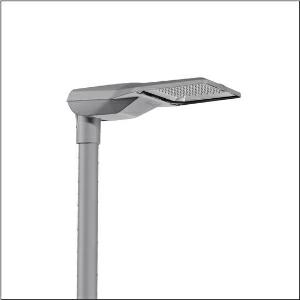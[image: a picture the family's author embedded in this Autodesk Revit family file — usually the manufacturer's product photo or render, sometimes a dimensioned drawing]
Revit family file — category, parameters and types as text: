
# Revit family: streetlight_sl_21_iq_midi___st1_0a_5xe3d31g08mb_3419
name_source: partatom
category: Lighting Fixtures
units: mm (PartAtom-declared; Revit-internal decimal feet)

## family parameters
Cut with Voids When Loaded = No
Host = Face
Light Source = No
Part Type = Normal
Room Calculation Point = No
Round Connector Dimension = Use Diameter
Shared = No

## types (1)
- --- (1 x LED, 19500 lm, 146.7 W, 3000K)
    Apparent Load = 147 VA
    CIE Flux Codes = 37 72 97 100 100
    Color Rendering = 70
    Color Temperature = 3000K
    Default Elevation = 1800 mm
    Description = Streetlight SL 21 iQ midi, mast luminaire, primary light control with lens, of PMMA, primary optical cover: cover, of toughened safety glass, transparent, light distribution: ST1.0a, light emission: direct distribution, primary light characteristic: asymmetric, installation type: post-top, side-entry, LED, High Power LED, rated luminous flux: 19.500lm, luminous efficacy: 133lm/W, light colour: 730, colour temperature: 3000K, control gear: iQ Street-Remote, control: Street-Remote, Auto-Match, Temp-Guard, Lumen-Switch, Night-Set, Smart-Wire, Light-Fading, Desk-Remote (wireless, voltage-free reading and setting of iQ features in the workshop via application-optimized NFC function/RFID function), optimised constant luminous flux control (CLO 2.0), pre-setting: linear dimming characteristic, mains connection: 230..240V, AC, 50/60Hz, start of lifetime: 147W, end of service life: 161W, reduction: 62W, luminaire housing, of diecast aluminium, powder-coated, Siteco® metallic grey (DB 702S), corrosivity category C5 high according to DIN EN ISO 12944, please order mast flange separately, inclination adjustable: 0°, 5°, 10°, 15°, sealing non-destructively replaceable, multi-level sealing system, length: 644mm, width: 335mm, height: 110mm, mast flange for spigot size: 42mm (side-entry): 5XC10008XM4, 60/48mm (side-entry/post-top): 5XC10108XM2, 76/60mm (side-entry/post-top): 5XC10108XM1, mounting height: 4..8m, protection rating (complete): IP66, insulation class (complete): insulation class II (safety insulation), certification: CE, ENEC, ENEC+, VDE, impact resistance: IK10, permissible operating ambient temperature for outdoor applications: -40..+50°C, standard-compliant lighting for roads and squares, packaging unit: 1 piece

Light Distribution: ST1.0a
    Height = 111 mm
    Lamp = 1 x LED
    Lamp Light Flux = 19500 lm
    Lamp Power = 146.7 W
    Lamp count = 1
    Length = 644 mm
    Luminous efficacy = 133 lm/W
    Manufacturer = Siteco
    ModVariant = No
    Model = 5XE3D31G08MB
    Number of Poles = 1
    OnlyDefault = Yes
    Power Factor = 1
    Product Name = Streetlight SL 21 iQ midi | ST1.0a
    Product group = mast luminaire | pylon top
    ProductGroupID = 6100
    Protection Class = Protection class II
    Protection Degree = IP 66
    RLX_Detail_Level = 1
    RLX_Emergency_Light_Flux = 0 lm
    RLX_Emergency_Type = 0
    RLX_Emergency_Type_DB = No
    RlxData = <blob elided: 26945 chars, md5=4b1ad950>
    Socket = socket
    Standby Power = 0 W
    System Light Flux = 19499 lm
    System Power = 147 W
    Type Comments = factory setting: luminous flux: 100 % | dim-lin: 254 | 753 mA
    Type Image = l_1004298.jpg
    URL = http://relux.com
    VarID = @adj_190741
    Voltage = 0 V
    Weight = 0.00 kg
    Width = 336 mm

## geometry (parser evidence)
native form markers: Blend x4, Sweep x13
no freeform markers — native parametric forms only
